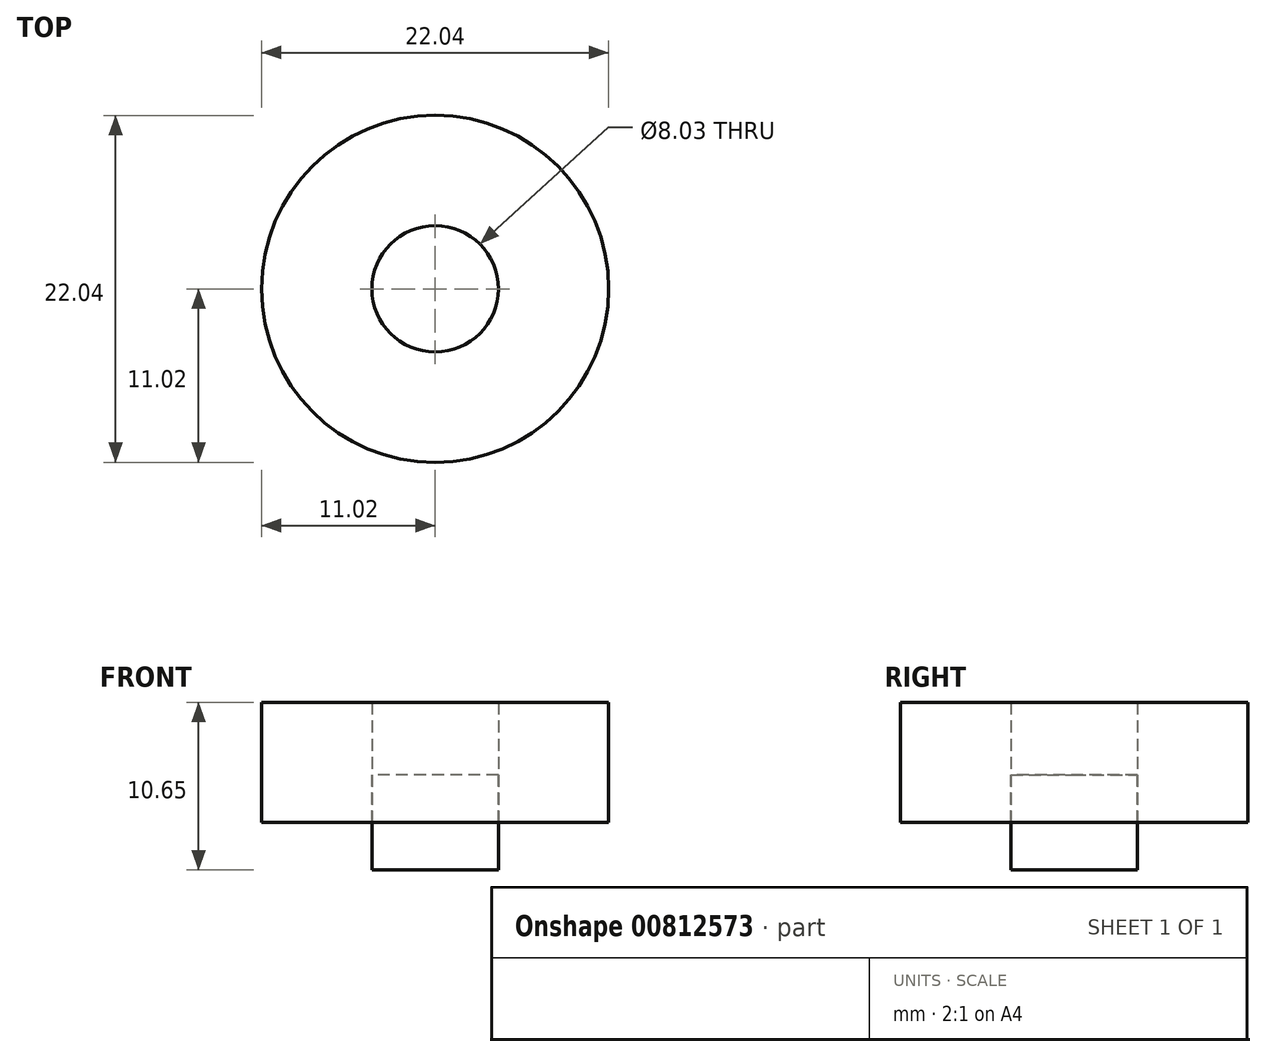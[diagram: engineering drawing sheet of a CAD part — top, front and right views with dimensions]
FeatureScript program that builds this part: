
annotation { "Feature Type Name" : "Feature", "Feature Type Description" : "" }
export const myFeature = defineFeature(function(context is Context, id is Id, definition is map)
    precondition{}
    {
        {
            var Q0;
            Q0=qCreatedBy(makeId("Top.planeOp"),FACE);
            var sketch = newSketch(context, id + "F0", { "sketchPlane" : qUnion([Q0])});
            skCircle(sketch, "E0", {"center": v(0, 0) * mm, "radius": 11.02 * mm});
            skCircle(sketch, "E1", {"center": v(0, 0) * mm, "radius": 4.01 * mm});
            skSolve(sketch);
        }
        {
            var Q0;
            Q0=makeQuery(id+"F0.imprint","IMPRINT",FACE,{"disambiguationData":[TD([[makeQuery(id+"F0.imprint","IMPRINT",EDGE,{"derivedFrom":sQuery(id+"F0.wireOp",EDGE,"E1")}),1.0]])]});
            extrude(context, id + "F1", {"entities" : qUnion([Q0]), "oppositeDirection" : true, "depth" : 6.06 * mm, "offsetDistance" : 25.4 * mm, "symmetric" : true});
        }
        {
            var Q0;
            Q0 = qSketchRegion(id + "F0", true);
            extrude(context, id + "F2", {"entities" : qUnion([Q0]), "depth" : 7.62 * mm, "offsetDistance" : 25.4 * mm});
        }
        {
            var Q0;
            Q0=makeQuery(id+"F1.opExtrude","CAP_FACE",FACE,{"disambiguationData":[OSD([sQuery(id+"F0.wireOp",EDGE,"E1")])],"isStart":true});
            var sketch = newSketch(context, id + "F3", { "sketchPlane" : qUnion([Q0])});
            skCircle(sketch, "E2", {"center": v(0, 0) * mm, "radius": 4.01 * mm});
            skSolve(sketch);
        }
        {
            var Q0;
            Q0 = qSketchRegion(id + "F3", true);
            extrude(context, id + "F4", {"entities" : qUnion([Q0]), "depth" : 4.57 * mm, "offsetDistance" : 25.4 * mm});
        }
    });
